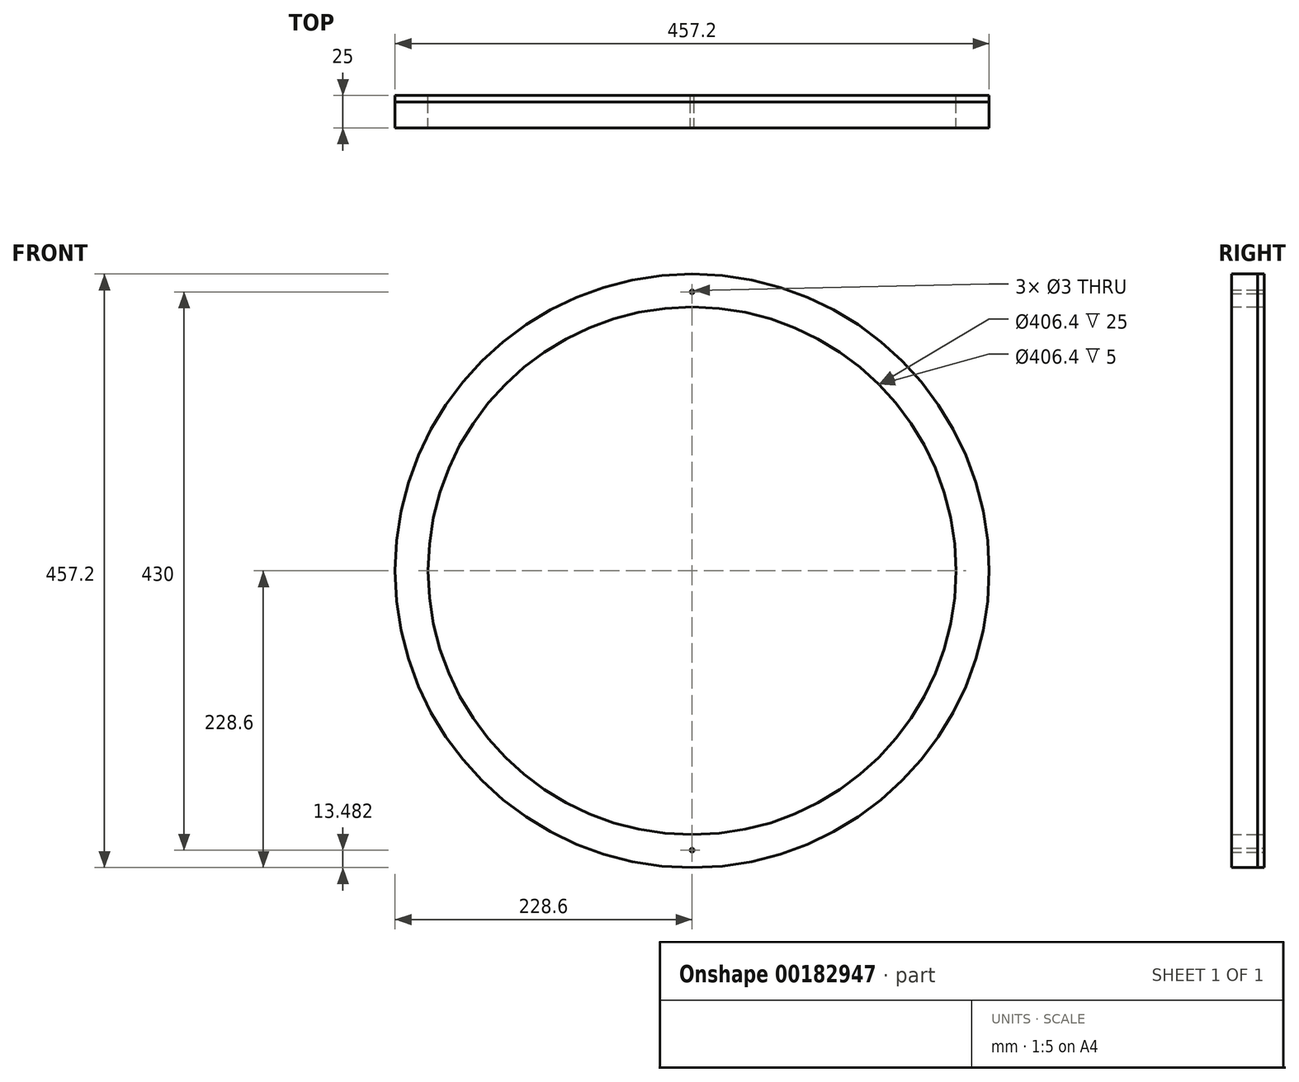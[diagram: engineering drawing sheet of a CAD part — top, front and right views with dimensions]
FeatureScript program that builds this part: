
annotation { "Feature Type Name" : "Feature", "Feature Type Description" : "" }
export const myFeature = defineFeature(function(context is Context, id is Id, definition is map)
    precondition{}
    {
        {
            var Q0;
            Q0=qCreatedBy(makeId("Front.planeOp"),FACE);
            var sketch = newSketch(context, id + "F0", { "sketchPlane" : qUnion([Q0])});
            skCircle(sketch, "E0", {"center": v(0, 0) * mm, "radius": 228.6 * mm});
            skCircle(sketch, "E1", {"center": v(0, 0) * mm, "radius": 203.2 * mm});
            skLineSegment(sketch, "E2", {"start": v(0, 238.57) * mm, "end": v(0, -228.6) * mm, "construction": true});
            skCircle(sketch, "E3", {"center": v(0, 214.88) * mm, "radius": 1.5 * mm});
            skCircle(sketch, "E4", {"center": v(0, -215.12) * mm, "radius": 1.5 * mm});
            skSolve(sketch);
        }
        {
            var Q0;
            Q0=makeQuery(id+"F0.imprint","IMPRINT",FACE,{"disambiguationData":[TD([[makeQuery(id+"F0.imprint","IMPRINT",EDGE,{"derivedFrom":sQuery(id+"F0.wireOp",EDGE,"E0")}),1.0]])]});
            var Q1;
            Q1=makeQuery(id+"F0.imprint","IMPRINT",FACE,{"disambiguationData":[TD([[makeQuery(id+"F0.imprint","IMPRINT",EDGE,{"derivedFrom":sQuery(id+"F0.wireOp",EDGE,"E4")}),1.0]])]});
            extrude(context, id + "F1", {"entities" : qUnion([Q0, Q1]), "depth" : 5 * mm});
        }
        {
            var Q0;
            Q0 = qSketchRegion(id + "F0", true);
            extrude(context, id + "F2", {"entities" : qUnion([Q0]), "depth" : 25 * mm});
        }
    });
